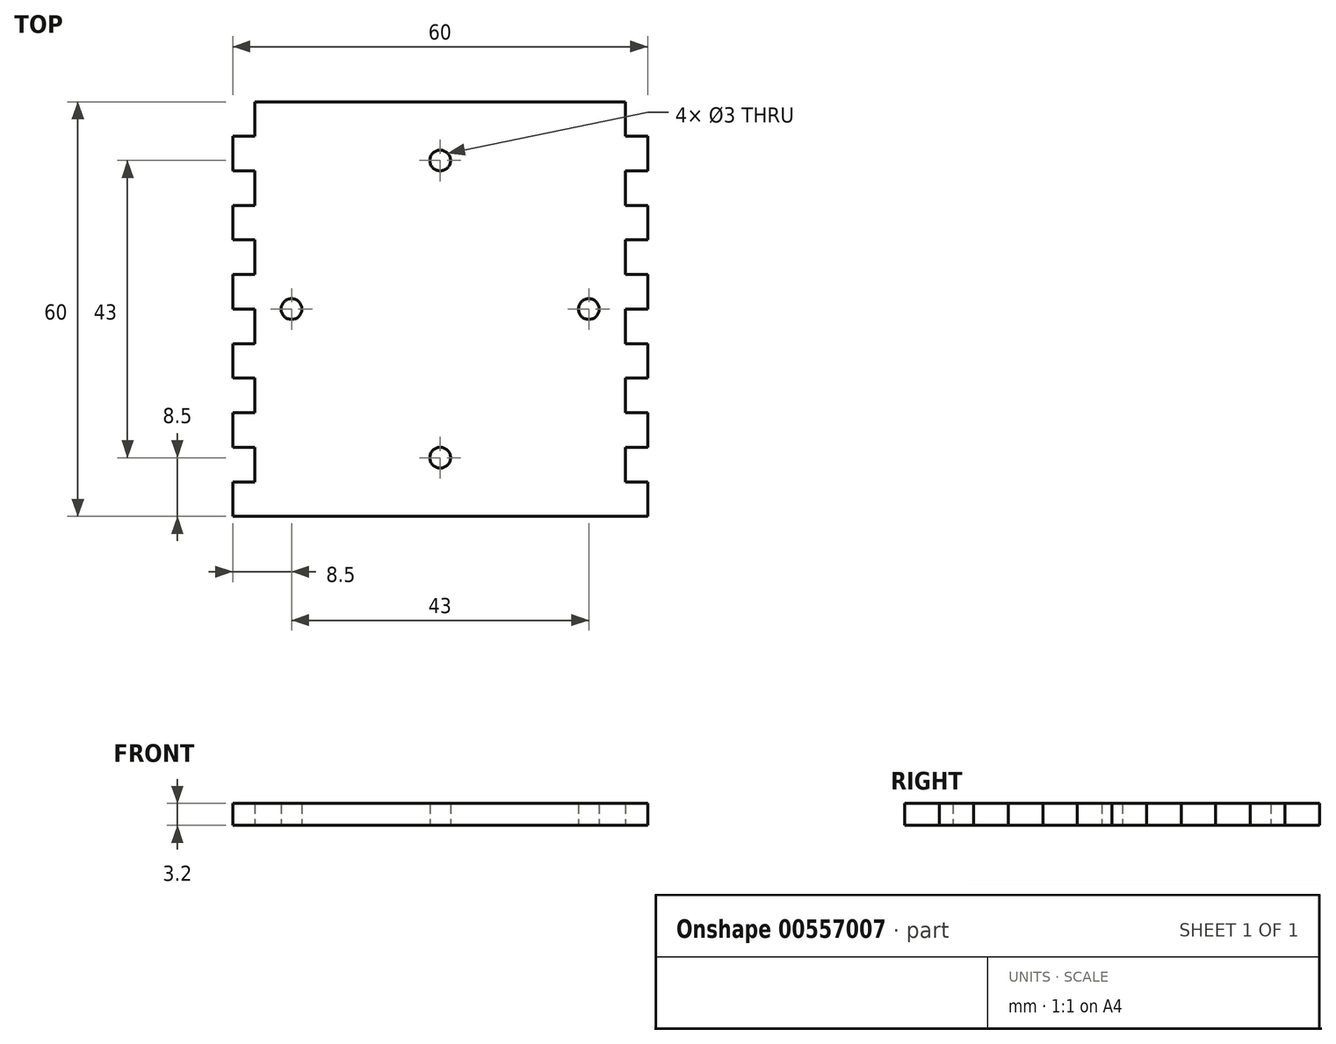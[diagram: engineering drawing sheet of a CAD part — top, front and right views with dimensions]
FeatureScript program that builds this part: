
annotation { "Feature Type Name" : "Feature", "Feature Type Description" : "" }
export const myFeature = defineFeature(function(context is Context, id is Id, definition is map)
    precondition{}
    {
        {
            var Q0;
            Q0=qCreatedBy(makeId("Top.planeOp"),FACE);
            var sketch = newSketch(context, id + "F0", { "sketchPlane" : qUnion([Q0])});
            skLineSegment(sketch, "E0.bottom", {"start": v(30, 30) * mm, "end": v(-26.8, 30) * mm});
            skLineSegment(sketch, "E0.top", {"start": v(30, -30) * mm, "end": v(-30, -30) * mm});
            skLineSegment(sketch, "E0.left", {"start": v(30, 25) * mm, "end": v(30, 20) * mm});
            skLineSegment(sketch, "E0.right", {"start": v(-30, 25) * mm, "end": v(-30, 20) * mm});
            skPoint(sketch, "E0.middle", {"position": v(0, 0) * mm});
            skLineSegment(sketch, "E1.bottom", {"start": v(26.8, 30) * mm, "end": v(30, 30) * mm});
            skLineSegment(sketch, "E1.top", {"start": v(26.8, 25) * mm, "end": v(30, 25) * mm});
            skLineSegment(sketch, "E1.left", {"start": v(26.8, 30) * mm, "end": v(26.8, 25) * mm});
            skLineSegment(sketch, "E2.bottom", {"start": v(26.8, 20) * mm, "end": v(30, 20) * mm});
            skLineSegment(sketch, "E2.top", {"start": v(26.8, 15) * mm, "end": v(30, 15) * mm});
            skLineSegment(sketch, "E2.left", {"start": v(26.8, 20) * mm, "end": v(26.8, 15) * mm});
            skLineSegment(sketch, "E3.bottom", {"start": v(26.8, 10) * mm, "end": v(30, 10) * mm});
            skLineSegment(sketch, "E3.top", {"start": v(26.8, 5) * mm, "end": v(30, 5) * mm});
            skLineSegment(sketch, "E3.left", {"start": v(26.8, 10) * mm, "end": v(26.8, 5) * mm});
            skLineSegment(sketch, "E4.bottom", {"start": v(26.8, 0) * mm, "end": v(30, 0) * mm});
            skLineSegment(sketch, "E4.top", {"start": v(26.8, -5) * mm, "end": v(30, -5) * mm});
            skLineSegment(sketch, "E4.left", {"start": v(26.8, 0) * mm, "end": v(26.8, -5) * mm});
            skLineSegment(sketch, "E5.bottom", {"start": v(26.8, -10) * mm, "end": v(30, -10) * mm});
            skLineSegment(sketch, "E5.top", {"start": v(26.8, -15) * mm, "end": v(30, -15) * mm});
            skLineSegment(sketch, "E5.left", {"start": v(26.8, -10) * mm, "end": v(26.8, -15) * mm});
            skLineSegment(sketch, "E6.bottom", {"start": v(26.8, -20) * mm, "end": v(30, -20) * mm});
            skLineSegment(sketch, "E6.top", {"start": v(26.8, -25) * mm, "end": v(30, -25) * mm});
            skLineSegment(sketch, "E6.left", {"start": v(26.8, -20) * mm, "end": v(26.8, -25) * mm});
            skLineSegment(sketch, "E7.trimOffspring", {"start": v(30, 15) * mm, "end": v(30, 10) * mm});
            skLineSegment(sketch, "E8.trimOffspring", {"start": v(30, 5) * mm, "end": v(30, 0) * mm});
            skLineSegment(sketch, "E9.trimOffspring", {"start": v(30, -5) * mm, "end": v(30, -10) * mm});
            skLineSegment(sketch, "E10.trimOffspring", {"start": v(30, -15) * mm, "end": v(30, -20) * mm});
            skLineSegment(sketch, "E11.trimOffspring", {"start": v(30, -25) * mm, "end": v(30, -30) * mm});
            skLineSegment(sketch, "E12.top", {"start": v(-30, 25) * mm, "end": v(-26.8, 25) * mm});
            skLineSegment(sketch, "E12.right", {"start": v(-26.8, 30) * mm, "end": v(-26.8, 25) * mm});
            skLineSegment(sketch, "E13.bottom", {"start": v(-30, 20) * mm, "end": v(-26.8, 20) * mm});
            skLineSegment(sketch, "E13.top", {"start": v(-30, 15) * mm, "end": v(-26.8, 15) * mm});
            skLineSegment(sketch, "E13.right", {"start": v(-26.8, 20) * mm, "end": v(-26.8, 15) * mm});
            skLineSegment(sketch, "E14.bottom", {"start": v(-30, 10) * mm, "end": v(-26.8, 10) * mm});
            skLineSegment(sketch, "E14.top", {"start": v(-30, 5) * mm, "end": v(-26.8, 5) * mm});
            skLineSegment(sketch, "E14.right", {"start": v(-26.8, 10) * mm, "end": v(-26.8, 5) * mm});
            skLineSegment(sketch, "E15.bottom", {"start": v(-30, 0) * mm, "end": v(-26.8, 0) * mm});
            skLineSegment(sketch, "E15.top", {"start": v(-30, -5) * mm, "end": v(-26.8, -5) * mm});
            skLineSegment(sketch, "E15.right", {"start": v(-26.8, 0) * mm, "end": v(-26.8, -5) * mm});
            skLineSegment(sketch, "E16.bottom", {"start": v(-30, -10) * mm, "end": v(-26.8, -10) * mm});
            skLineSegment(sketch, "E16.top", {"start": v(-30, -15) * mm, "end": v(-26.8, -15) * mm});
            skLineSegment(sketch, "E16.right", {"start": v(-26.8, -10) * mm, "end": v(-26.8, -15) * mm});
            skLineSegment(sketch, "E17.bottom", {"start": v(-30, -20) * mm, "end": v(-26.8, -20) * mm});
            skLineSegment(sketch, "E17.top", {"start": v(-30, -25) * mm, "end": v(-26.8, -25) * mm});
            skLineSegment(sketch, "E17.right", {"start": v(-26.8, -20) * mm, "end": v(-26.8, -25) * mm});
            skPoint(sketch, "E18.orphan", {"position": v(-30, 30) * mm});
            skLineSegment(sketch, "E19.trimOffspring", {"start": v(-30, 15) * mm, "end": v(-30, 10) * mm});
            skLineSegment(sketch, "E20.trimOffspring", {"start": v(-30, 5) * mm, "end": v(-30, 0) * mm});
            skLineSegment(sketch, "E21.trimOffspring", {"start": v(-30, -5) * mm, "end": v(-30, -10) * mm});
            skLineSegment(sketch, "E22.trimOffspring", {"start": v(-30, -15) * mm, "end": v(-30, -20) * mm});
            skLineSegment(sketch, "E23.trimOffspring", {"start": v(-30, -25) * mm, "end": v(-30, -30) * mm});
            skCircle(sketch, "E24", {"center": v(0, 21.5) * mm, "radius": 1.5 * mm});
            skCircle(sketch, "E25", {"center": v(0, -21.5) * mm, "radius": 1.5 * mm});
            skCircle(sketch, "E26", {"center": v(21.5, 0) * mm, "radius": 1.5 * mm});
            skCircle(sketch, "E27", {"center": v(-21.5, 0) * mm, "radius": 1.5 * mm});
            skSolve(sketch);
        }
        {
            var Q0;
            Q0=qSketchRegion(id+"F0",true);
            extrude(context, id + "F1", {"entities" : qUnion([Q0]), "depth" : 3.2 * mm});
        }
    });
